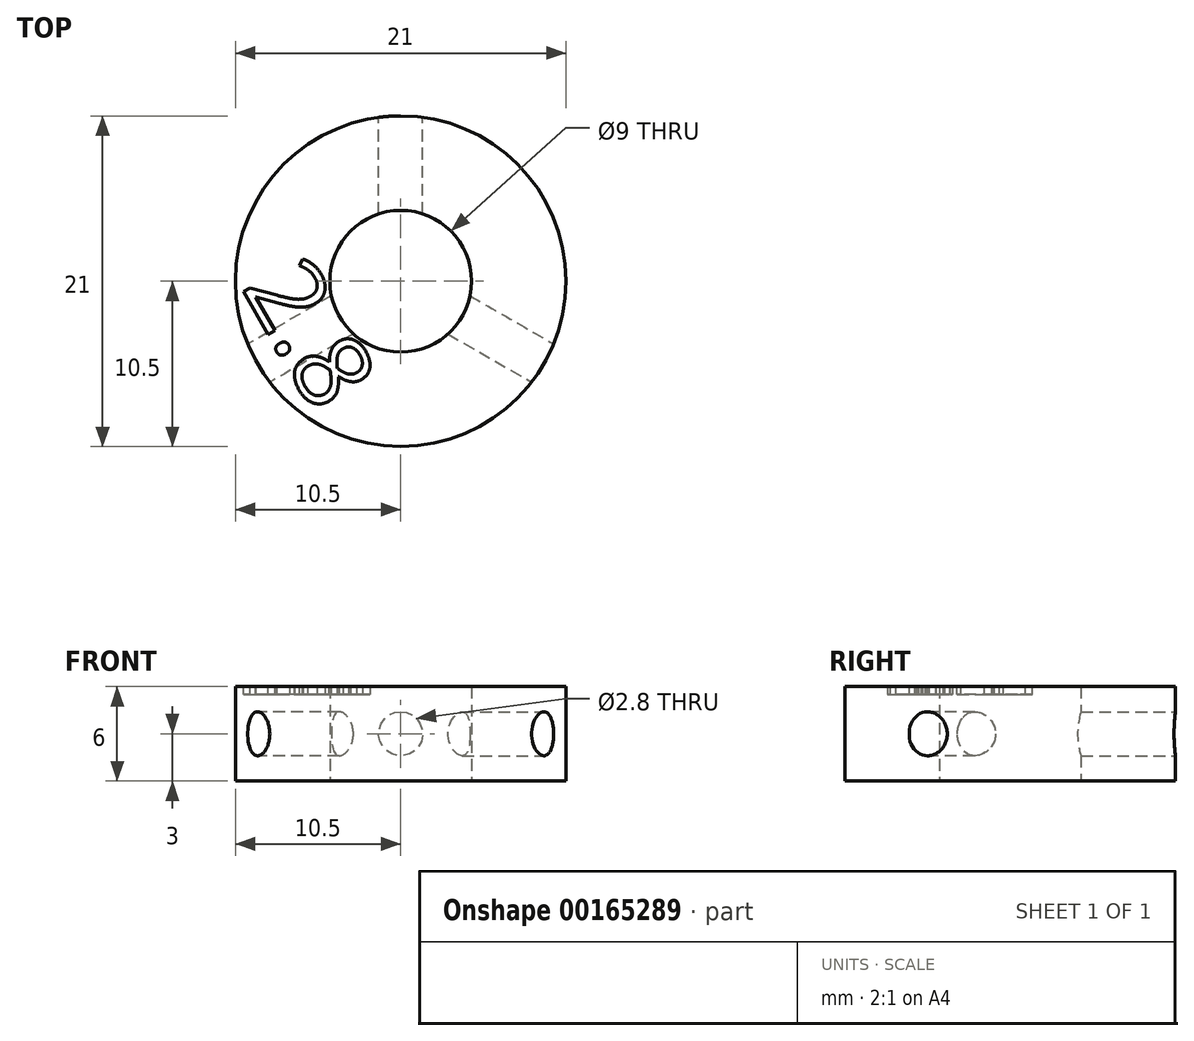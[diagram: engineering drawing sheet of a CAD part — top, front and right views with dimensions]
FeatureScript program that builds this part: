
annotation { "Feature Type Name" : "Feature", "Feature Type Description" : "" }
export const myFeature = defineFeature(function(context is Context, id is Id, definition is map)
    precondition{}
    {
        {
            var Q0;
            Q0=qCreatedBy(makeId("Top.planeOp"),FACE);
            var sketch = newSketch(context, id + "F0", { "sketchPlane" : qUnion([Q0])});
            skCircle(sketch, "E0", {"center": v(0, 0) * mm, "radius": 4.5 * mm});
            skCircle(sketch, "E1", {"center": v(0, 0) * mm, "radius": 10.5 * mm});
            skSolve(sketch);
        }
        {
            var Q0;
            Q0=makeQuery(id+"F0.imprint","IMPRINT",FACE,{"disambiguationData":[TD([[makeQuery(id+"F0.imprint","IMPRINT",EDGE,{"derivedFrom":sQuery(id+"F0.wireOp",EDGE,"E0")}),-1.0]])]});
            extrude(context, id + "F1", {"entities" : qUnion([Q0]), "depth" : 6 * mm});
        }
        {
            var Q0;
            Q0=qCreatedBy(makeId("Top.planeOp"),FACE);
            cPlane(context, id + "F2", {"entities" : qUnion([Q0]), "cplaneType" : CPlaneType.OFFSET, "offset" : 3 * mm, "width" : 150 * mm, "height" : 150 * mm});
        }
        {
            var Q0;
            Q0=qCreatedBy(id+"F2.planeOp",FACE);
            var sketch = newSketch(context, id + "F3", { "sketchPlane" : qUnion([Q0])});
            skLineSegment(sketch, "E2", {"start": v(0, 0) * mm, "end": v(0, 10.5) * mm, "construction": true});
            skLineSegment(sketch, "E3", {"start": v(9.1, -5.25) * mm, "end": v(0, 0) * mm, "construction": true});
            skLineSegment(sketch, "E4", {"start": v(0, 0) * mm, "end": v(-9.1, -5.25) * mm, "construction": true});
            skSolve(sketch);
        }
        {
            var Q0;
            Q0=sQuery(id+"F3.wireOp",EDGE,"E4");
            var Q1;
            Q1=sQuery(id+"F3.wireOp",VERTEX,"E4.end");
            cPlane(context, id + "F4", {"entities" : qUnion([Q0, Q1]), "cplaneType" : CPlaneType.LINE_POINT, "offset" : 25 * mm, "width" : 150 * mm, "height" : 150 * mm});
        }
        {
            var Q0;
            Q0=sQuery(id+"F3.wireOp",EDGE,"E3");
            var Q1;
            Q1=sQuery(id+"F3.wireOp",VERTEX,"E3.start");
            cPlane(context, id + "F5", {"entities" : qUnion([Q0, Q1]), "cplaneType" : CPlaneType.LINE_POINT, "offset" : 25 * mm, "width" : 150 * mm, "height" : 150 * mm});
        }
        {
            var Q0;
            Q0=sQuery(id+"F3.wireOp",EDGE,"E2");
            var Q1;
            Q1=sQuery(id+"F3.wireOp",VERTEX,"E2.end");
            cPlane(context, id + "F6", {"entities" : qUnion([Q0, Q1]), "cplaneType" : CPlaneType.LINE_POINT, "offset" : 25 * mm, "width" : 150 * mm, "height" : 150 * mm});
        }
        {
            var Q0;
            Q0=qCreatedBy(id+"F5.planeOp",FACE);
            var sketch = newSketch(context, id + "F7", { "sketchPlane" : qUnion([Q0])});
            skPoint(sketch, "E5.0", {"position": v(0, 3) * mm});
            skCircle(sketch, "E6", {"center": v(0, 3) * mm, "radius": 1.4 * mm});
            skSolve(sketch);
        }
        {
            var Q0;
            Q0=qCreatedBy(id+"F4.planeOp",FACE);
            var sketch = newSketch(context, id + "F8", { "sketchPlane" : qUnion([Q0])});
            skPoint(sketch, "E7.0", {"position": v(0, 3) * mm});
            skCircle(sketch, "E8", {"center": v(0, 3) * mm, "radius": 1.4 * mm});
            skSolve(sketch);
        }
        {
            var Q0;
            Q0=qCreatedBy(id+"F6.planeOp",FACE);
            var sketch = newSketch(context, id + "F9", { "sketchPlane" : qUnion([Q0])});
            skPoint(sketch, "E9.0", {"position": v(0, 3) * mm});
            skCircle(sketch, "E10", {"center": v(0, 3) * mm, "radius": 1.4 * mm});
            skSolve(sketch);
        }
        {
            var Q0;
            Q0=makeQuery(id+"F7.imprint","IMPRINT",FACE,{"disambiguationData":[TD([[makeQuery(id+"F7.imprint","IMPRINT",EDGE,{"derivedFrom":sQuery(id+"F7.wireOp",EDGE,"E6")}),1.0]])]});
            var Q1;
            Q1=makeQuery(id+"F1.opExtrude","SWEPT_FACE",FACE,{"disambiguationData":[OSD([sQuery(id+"F0.wireOp",EDGE,"E0")])]});
            extrude(context, id + "F10", {"entities" : qUnion([Q0]), "operationType" : NewBodyOperationType.REMOVE, "endBound" : BoundingType.UP_TO_SURFACE, "endBoundEntityFace" : qUnion([Q1]), "depth" : 25 * mm});
        }
        {
            var Q0;
            Q0=makeQuery(id+"F8.imprint","IMPRINT",FACE,{"disambiguationData":[TD([[makeQuery(id+"F8.imprint","IMPRINT",EDGE,{"derivedFrom":sQuery(id+"F8.wireOp",EDGE,"E8")}),1.0]])]});
            var Q1;
            Q1=makeQuery(id+"F1.opExtrude","SWEPT_FACE",FACE,{"disambiguationData":[OSD([sQuery(id+"F0.wireOp",EDGE,"E0")])]});
            extrude(context, id + "F11", {"entities" : qUnion([Q0]), "operationType" : NewBodyOperationType.REMOVE, "endBound" : BoundingType.UP_TO_SURFACE, "oppositeDirection" : true, "endBoundEntityFace" : qUnion([Q1]), "depth" : 25 * mm});
        }
        {
            var Q0;
            Q0=makeQuery(id+"F9.imprint","IMPRINT",FACE,{"disambiguationData":[TD([[makeQuery(id+"F9.imprint","IMPRINT",EDGE,{"derivedFrom":sQuery(id+"F9.wireOp",EDGE,"E10")}),1.0]])]});
            var Q1;
            Q1=makeQuery(id+"F1.opExtrude","SWEPT_FACE",FACE,{"disambiguationData":[OSD([sQuery(id+"F0.wireOp",EDGE,"E0")])]});
            extrude(context, id + "F12", {"entities" : qUnion([Q0]), "operationType" : NewBodyOperationType.REMOVE, "endBound" : BoundingType.UP_TO_SURFACE, "oppositeDirection" : true, "endBoundEntityFace" : qUnion([Q1]), "depth" : 25 * mm});
        }
        {
            var Q0;
            Q0=makeQuery(id+"F1.opExtrude","CAP_FACE",FACE,{"disambiguationData":[OSD([sQuery(id+"F0.wireOp",EDGE,"E0"),sQuery(id+"F0.wireOp",EDGE,"E1")])],"isStart":false});
            var sketch = newSketch(context, id + "F13", { "sketchPlane" : qUnion([Q0])});
            skText(sketch, "E11", { "text": "2.8\n", "fontName": "OpenSans-Regular.ttf"});
            const initialGuessF13  = {"E11": [-0.01014, -0.00039, 0.5, -0.86603, 0.0048]};
            skSetInitialGuess(sketch, initialGuessF13);
            skSolve(sketch);
        }
        {
            var Q0;
            Q0 = qSketchRegion(id + "F13", true);
            extrude(context, id + "F14", {"entities" : qUnion([Q0]), "operationType" : NewBodyOperationType.REMOVE, "oppositeDirection" : true, "depth" : 0.5 * mm});
        }
    });
